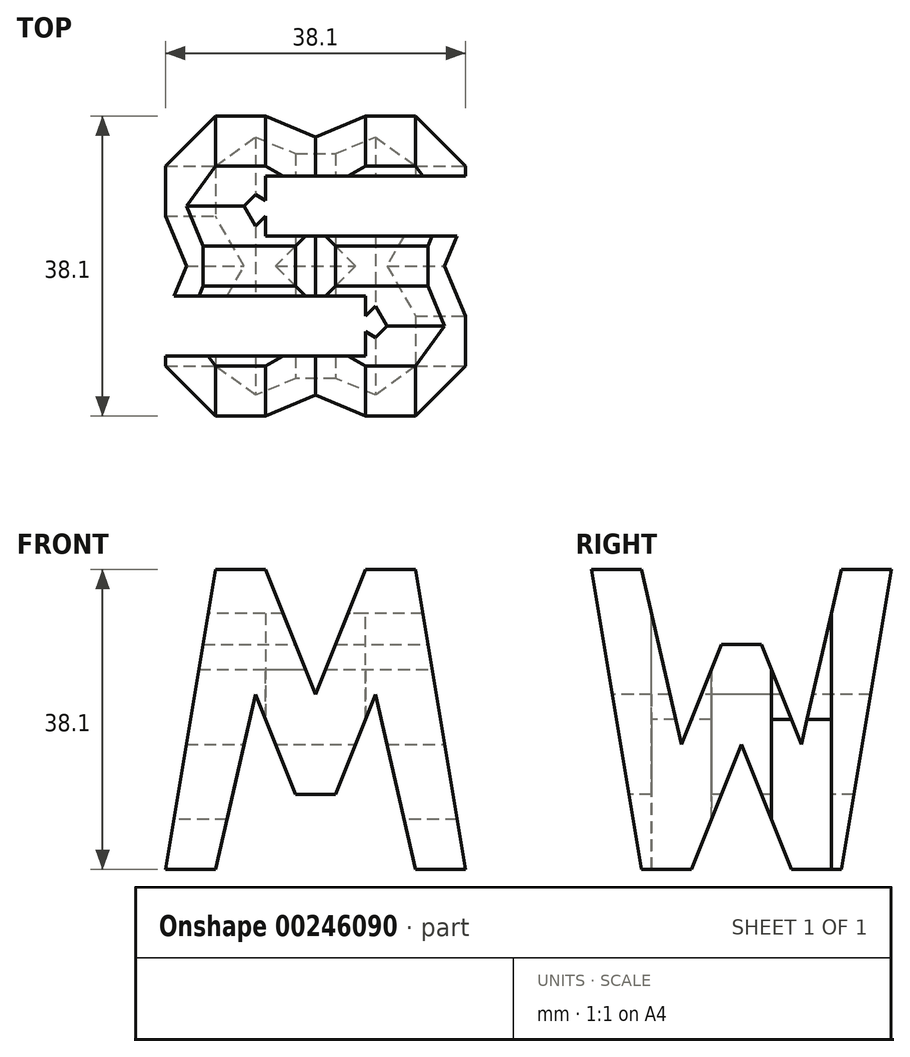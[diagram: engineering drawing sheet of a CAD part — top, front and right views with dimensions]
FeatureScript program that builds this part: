
annotation { "Feature Type Name" : "Feature", "Feature Type Description" : "" }
export const myFeature = defineFeature(function(context is Context, id is Id, definition is map)
    precondition{}
    {
        {
            var Q0;
            Q0=qCreatedBy(makeId("Front.planeOp"),FACE);
            var sketch = newSketch(context, id + "F0", { "sketchPlane" : qUnion([Q0])});
            skLineSegment(sketch, "E0", {"start": v(0, 0) * mm, "end": v(0, 38.1) * mm});
            skLineSegment(sketch, "E1", {"start": v(0, 0) * mm, "end": v(38.1, 0) * mm});
            skLineSegment(sketch, "E2", {"start": v(0, 38.1) * mm, "end": v(38.1, 38.1) * mm});
            skLineSegment(sketch, "E3", {"start": v(38.1, 38.1) * mm, "end": v(38.1, 0) * mm});
            skSolve(sketch);
        }
        {
            var Q0;
            Q0=qCreatedBy(makeId("Front.planeOp"),FACE);
            cPlane(context, id + "F1", {"entities" : qUnion([Q0]), "cplaneType" : CPlaneType.OFFSET, "offset" : 38.1 * mm, "width" : 152.4 * mm, "height" : 152.4 * mm});
        }
        {
            var Q0;
            Q0=qCreatedBy(makeId("Right.planeOp"),FACE);
            cPlane(context, id + "F2", {"entities" : qUnion([Q0]), "cplaneType" : CPlaneType.OFFSET, "offset" : 38.1 * mm, "width" : 152.4 * mm, "height" : 152.4 * mm});
        }
        {
            var Q0;
            Q0=qCreatedBy(makeId("Top.planeOp"),FACE);
            cPlane(context, id + "F3", {"entities" : qUnion([Q0]), "cplaneType" : CPlaneType.OFFSET, "offset" : 38.1 * mm, "width" : 152.4 * mm, "height" : 152.4 * mm});
        }
        {
            var Q0;
            Q0=qCreatedBy(id+"F2.planeOp",FACE);
            var sketch = newSketch(context, id + "F4", { "sketchPlane" : qUnion([Q0])});
            skLineSegment(sketch, "E4", {"start": v(-38.1, 38.1) * mm, "end": v(-31.75, 0) * mm});
            skLineSegment(sketch, "E5", {"start": v(-31.75, 0) * mm, "end": v(-25.4, 0) * mm});
            skLineSegment(sketch, "E6", {"start": v(-25.4, 0) * mm, "end": v(-19.05, 15.88) * mm});
            skLineSegment(sketch, "E7", {"start": v(-19.05, 15.88) * mm, "end": v(-12.7, 0) * mm});
            skLineSegment(sketch, "E8", {"start": v(-12.7, 0) * mm, "end": v(-6.35, 0) * mm});
            skLineSegment(sketch, "E9", {"start": v(-6.35, 0) * mm, "end": v(0, 38.1) * mm});
            skLineSegment(sketch, "E10", {"start": v(0, 38.1) * mm, "end": v(-6.35, 38.1) * mm});
            skLineSegment(sketch, "E11", {"start": v(-6.35, 38.1) * mm, "end": v(-11.43, 15.88) * mm});
            skLineSegment(sketch, "E12", {"start": v(-11.43, 15.87) * mm, "end": v(-16.51, 28.58) * mm});
            skLineSegment(sketch, "E13", {"start": v(-16.51, 28.58) * mm, "end": v(-21.6, 28.58) * mm});
            skLineSegment(sketch, "E14", {"start": v(-21.6, 28.58) * mm, "end": v(-26.67, 15.87) * mm});
            skLineSegment(sketch, "E15", {"start": v(-26.67, 15.88) * mm, "end": v(-31.75, 38.1) * mm});
            skLineSegment(sketch, "E16", {"start": v(-38.1, 38.1) * mm, "end": v(-31.75, 38.1) * mm});
            skLineSegment(sketch, "E17.bottom", {"start": v(0, 0) * mm, "end": v(-38.1, 0) * mm});
            skLineSegment(sketch, "E17.top", {"start": v(0, 38.1) * mm, "end": v(-38.1, 38.1) * mm});
            skLineSegment(sketch, "E17.left", {"start": v(0, 0) * mm, "end": v(0, 38.1) * mm});
            skLineSegment(sketch, "E17.right", {"start": v(-38.1, 0) * mm, "end": v(-38.1, 38.1) * mm});
            skSolve(sketch);
        }
        {
            var Q0;
            Q0=qCreatedBy(id+"F1.planeOp",FACE);
            var sketch = newSketch(context, id + "F5", { "sketchPlane" : qUnion([Q0])});
            skLineSegment(sketch, "E18", {"start": v(0, 0) * mm, "end": v(6.35, 38.1) * mm});
            skLineSegment(sketch, "E19", {"start": v(6.35, 38.1) * mm, "end": v(12.7, 38.1) * mm});
            skLineSegment(sketch, "E20", {"start": v(12.7, 38.1) * mm, "end": v(19.05, 22.23) * mm});
            skLineSegment(sketch, "E21", {"start": v(19.05, 22.23) * mm, "end": v(25.4, 38.1) * mm});
            skLineSegment(sketch, "E22", {"start": v(25.4, 38.1) * mm, "end": v(31.75, 38.1) * mm});
            skLineSegment(sketch, "E23", {"start": v(31.75, 38.1) * mm, "end": v(38.1, 0) * mm});
            skLineSegment(sketch, "E24", {"start": v(38.1, 0) * mm, "end": v(31.75, 0) * mm});
            skLineSegment(sketch, "E25", {"start": v(31.75, 0) * mm, "end": v(26.67, 22.23) * mm});
            skLineSegment(sketch, "E26", {"start": v(26.67, 22.23) * mm, "end": v(21.59, 9.52) * mm});
            skLineSegment(sketch, "E27", {"start": v(21.6, 9.53) * mm, "end": v(16.51, 9.53) * mm});
            skLineSegment(sketch, "E28", {"start": v(16.51, 9.52) * mm, "end": v(11.43, 22.23) * mm});
            skLineSegment(sketch, "E29", {"start": v(11.43, 22.23) * mm, "end": v(6.35, 0) * mm});
            skLineSegment(sketch, "E30", {"start": v(6.35, 0) * mm, "end": v(0, 0) * mm});
            skLineSegment(sketch, "E31.bottom", {"start": v(0, 0) * mm, "end": v(38.1, 0) * mm});
            skLineSegment(sketch, "E31.top", {"start": v(0, 38.1) * mm, "end": v(38.1, 38.1) * mm});
            skLineSegment(sketch, "E31.left", {"start": v(0, 0) * mm, "end": v(0, 38.1) * mm});
            skLineSegment(sketch, "E31.right", {"start": v(38.1, 0) * mm, "end": v(38.1, 38.1) * mm});
            skSolve(sketch);
        }
        {
            var Q0;
            Q0 = qSketchRegion(id + "F0", true);
            extrude(context, id + "F6", {"entities" : qUnion([Q0]), "depth" : 38.1 * mm});
        }
        {
            var Q0;
            {var subQ0=sQuery(id+"F4.wireOp",EDGE,"E4");Q0=makeQuery(id+"F4.imprint","IMPRINT",FACE,{"disambiguationData":[TD([[makeQuery(id+"F4.imprint","IMPRINT",EDGE,{"derivedFrom":subQ0}),-1.0]])]});}
            var Q1;
            {var subQ0=sQuery(id+"F4.wireOp",EDGE,"E11");Q1=makeQuery(id+"F4.imprint","IMPRINT",FACE,{"disambiguationData":[TD([[makeQuery(id+"F4.imprint","IMPRINT",EDGE,{"derivedFrom":subQ0}),-1.0]])]});}
            var Q2;
            {var subQ0=sQuery(id+"F4.wireOp",EDGE,"E6");Q2=makeQuery(id+"F4.imprint","IMPRINT",FACE,{"disambiguationData":[TD([[makeQuery(id+"F4.imprint","IMPRINT",EDGE,{"derivedFrom":subQ0}),-1.0]])]});}
            var Q3;
            {var subQ0=sQuery(id+"F4.wireOp",EDGE,"E9");Q3=makeQuery(id+"F4.imprint","IMPRINT",FACE,{"disambiguationData":[TD([[makeQuery(id+"F4.imprint","IMPRINT",EDGE,{"derivedFrom":subQ0}),-1.0]])]});}
            extrude(context, id + "F7", {"entities" : qUnion([Q0, Q1, Q2, Q3]), "operationType" : NewBodyOperationType.REMOVE, "oppositeDirection" : true, "depth" : 38.1 * mm});
        }
        {
            var Q0;
            {var subQ0=sQuery(id+"F5.wireOp",EDGE,"E18");Q0=makeQuery(id+"F5.imprint","IMPRINT",FACE,{"disambiguationData":[TD([[makeQuery(id+"F5.imprint","IMPRINT",EDGE,{"derivedFrom":subQ0}),1.0]])]});}
            var Q1;
            {var subQ0=sQuery(id+"F5.wireOp",EDGE,"E20");Q1=makeQuery(id+"F5.imprint","IMPRINT",FACE,{"disambiguationData":[TD([[makeQuery(id+"F5.imprint","IMPRINT",EDGE,{"derivedFrom":subQ0}),1.0]])]});}
            var Q2;
            {var subQ0=sQuery(id+"F5.wireOp",EDGE,"E23");Q2=makeQuery(id+"F5.imprint","IMPRINT",FACE,{"disambiguationData":[TD([[makeQuery(id+"F5.imprint","IMPRINT",EDGE,{"derivedFrom":subQ0}),1.0]])]});}
            var Q3;
            {var subQ0=sQuery(id+"F5.wireOp",EDGE,"E25");Q3=makeQuery(id+"F5.imprint","IMPRINT",FACE,{"disambiguationData":[TD([[makeQuery(id+"F5.imprint","IMPRINT",EDGE,{"derivedFrom":subQ0}),1.0]])]});}
            extrude(context, id + "F8", {"entities" : qUnion([Q0, Q1, Q2, Q3]), "operationType" : NewBodyOperationType.REMOVE, "oppositeDirection" : true, "depth" : 38.1 * mm});
        }
        {
            var Q0;
            Q0=qCreatedBy(id+"F3.planeOp",FACE);
            var sketch = newSketch(context, id + "F9", { "sketchPlane" : qUnion([Q0])});
            skLineSegment(sketch, "E32.bottom", {"start": v(0, 0) * mm, "end": v(38.1, 0) * mm});
            skLineSegment(sketch, "E32.top", {"start": v(0, -38.1) * mm, "end": v(38.1, -38.1) * mm});
            skLineSegment(sketch, "E32.left", {"start": v(0, 0) * mm, "end": v(0, -38.1) * mm});
            skLineSegment(sketch, "E32.right", {"start": v(38.1, 0) * mm, "end": v(38.1, -38.1) * mm});
            skLineSegment(sketch, "E33", {"start": v(38.1, -7.62) * mm, "end": v(12.7, -7.62) * mm});
            skLineSegment(sketch, "E34", {"start": v(12.7, -7.62) * mm, "end": v(12.7, -15.24) * mm});
            skLineSegment(sketch, "E35", {"start": v(12.7, -15.24) * mm, "end": v(38.1, -15.24) * mm});
            skLineSegment(sketch, "E36", {"start": v(0, -22.86) * mm, "end": v(25.4, -22.86) * mm});
            skLineSegment(sketch, "E37", {"start": v(25.4, -22.86) * mm, "end": v(25.4, -30.48) * mm});
            skLineSegment(sketch, "E38", {"start": v(25.4, -30.48) * mm, "end": v(0, -30.48) * mm});
            skSolve(sketch);
        }
        {
            var Q0;
            {var subQ0=sQuery(id+"F9.wireOp",EDGE,"E33");Q0=makeQuery(id+"F9.imprint","IMPRINT",FACE,{"disambiguationData":[TD([[makeQuery(id+"F9.imprint","IMPRINT",EDGE,{"derivedFrom":subQ0}),1.0]])]});}
            var Q1;
            {var subQ0=sQuery(id+"F9.wireOp",EDGE,"E36");Q1=makeQuery(id+"F9.imprint","IMPRINT",FACE,{"disambiguationData":[TD([[makeQuery(id+"F9.imprint","IMPRINT",EDGE,{"derivedFrom":subQ0}),-1.0]])]});}
            extrude(context, id + "F10", {"entities" : qUnion([Q0, Q1]), "operationType" : NewBodyOperationType.REMOVE, "oppositeDirection" : true, "depth" : 38.1 * mm});
        }
    });
